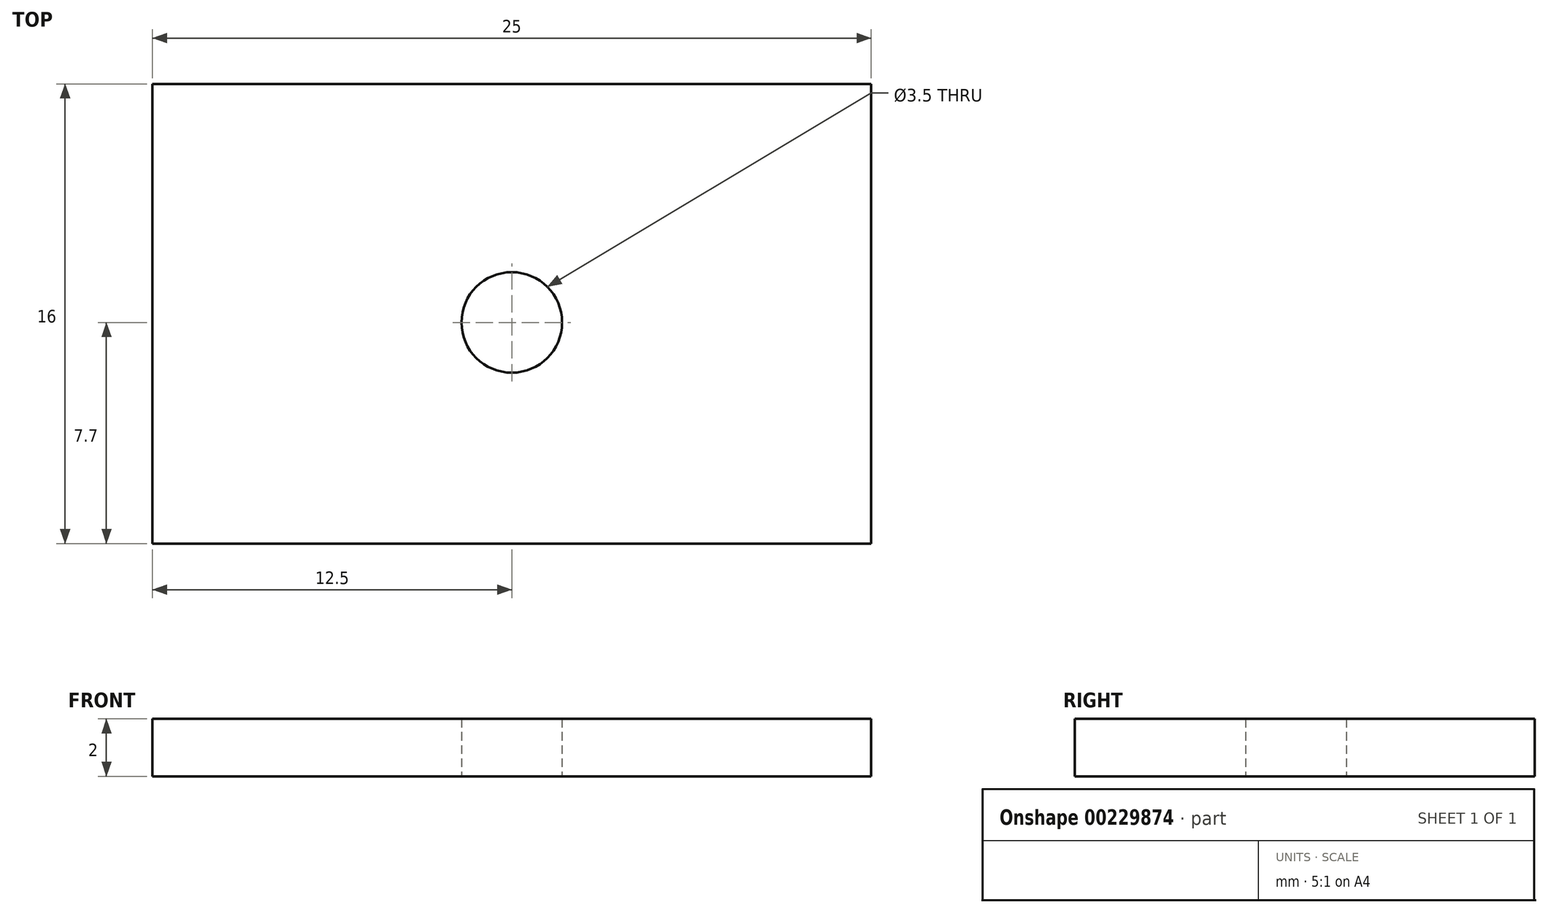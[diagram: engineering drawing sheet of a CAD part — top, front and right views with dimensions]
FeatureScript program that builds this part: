
annotation { "Feature Type Name" : "Feature", "Feature Type Description" : "" }
export const myFeature = defineFeature(function(context is Context, id is Id, definition is map)
    precondition{}
    {
        {
            var Q0;
            Q0=qCreatedBy(makeId("Top.planeOp"),FACE);
            var sketch = newSketch(context, id + "F0", { "sketchPlane" : qUnion([Q0])});
            skLineSegment(sketch, "E0.bottom", {"start": v(0, 0) * mm, "end": v(25, 0) * mm});
            skLineSegment(sketch, "E0.top", {"start": v(0, 16) * mm, "end": v(25, 16) * mm});
            skLineSegment(sketch, "E0.left", {"start": v(0, 0) * mm, "end": v(0, 16) * mm});
            skLineSegment(sketch, "E0.right", {"start": v(25, 0) * mm, "end": v(25, 16) * mm});
            skCircle(sketch, "E1", {"center": v(12.5, 7.7) * mm, "radius": 1.75 * mm});
            skLineSegment(sketch, "E2", {"start": v(0, 2) * mm, "end": v(25, 2) * mm, "construction": true});
            skLineSegment(sketch, "E3", {"start": v(12.5, 0) * mm, "end": v(12.5, 16) * mm, "construction": true});
            skSolve(sketch);
        }
        {
            var Q0;
            Q0 = qSketchRegion(id + "F0", true);
            extrude(context, id + "F1", {"entities" : qUnion([Q0]), "depth" : 2 * mm});
        }
    });
